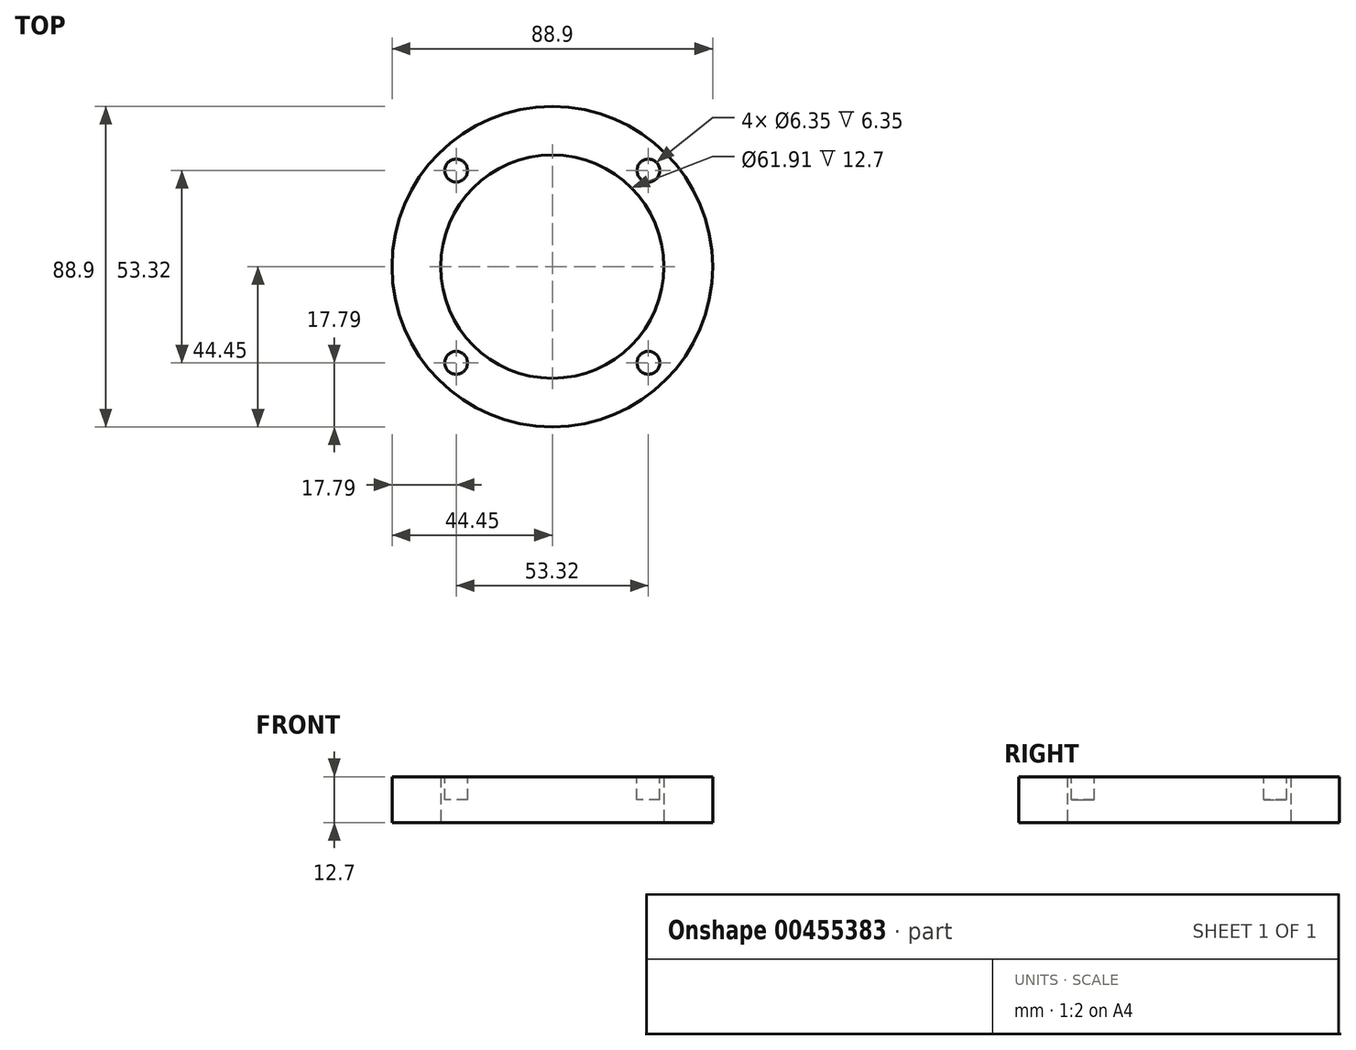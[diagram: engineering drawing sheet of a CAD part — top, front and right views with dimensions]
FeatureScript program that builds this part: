
annotation { "Feature Type Name" : "Feature", "Feature Type Description" : "" }
export const myFeature = defineFeature(function(context is Context, id is Id, definition is map)
    precondition{}
    {
        {
            var Q0;
            Q0=qCreatedBy(makeId("Top.planeOp"),FACE);
            var sketch = newSketch(context, id + "F0", { "sketchPlane" : qUnion([Q0])});
            skCircle(sketch, "E0", {"center": v(0, 0) * mm, "radius": 30.96 * mm});
            skCircle(sketch, "E1", {"center": v(0, 0) * mm, "radius": 44.45 * mm});
            skSolve(sketch);
        }
        {
            var Q0;
            Q0 = qSketchRegion(id + "F0", true);
            extrude(context, id + "F1", {"entities" : qUnion([Q0]), "depth" : 12.7 * mm});
        }
        {
            var Q0;
            Q0=makeQuery(id+"F1.opExtrude","CAP_FACE",FACE,{"disambiguationData":[OSD([sQuery(id+"F0.wireOp",EDGE,"E0"),sQuery(id+"F0.wireOp",EDGE,"E1")])],"isStart":false});
            var sketch = newSketch(context, id + "F2", { "sketchPlane" : qUnion([Q0])});
            skLineSegment(sketch, "E2", {"start": v(0, 0) * mm, "end": v(44.12, 44.12) * mm, "construction": true});
            skCircle(sketch, "E3", {"center": v(26.66, 26.66) * mm, "radius": 3.18 * mm});
            skLineSegment(sketch, "E4", {"start": v(21.89, 21.89) * mm, "end": v(31.43, 31.43) * mm, "construction": true});
            skCircle(sketch, "E5.1.0", {"center": v(-26.66, 26.66) * mm, "radius": 3.18 * mm});
            skCircle(sketch, "E5.2.0", {"center": v(-26.66, -26.66) * mm, "radius": 3.18 * mm});
            skCircle(sketch, "E5.3.0", {"center": v(26.66, -26.66) * mm, "radius": 3.18 * mm});
            skPoint(sketch, "E5.center", {"position": v(0, 0) * mm});
            skSolve(sketch);
        }
        {
            var Q0;
            Q0 = qSketchRegion(id + "F2", true);
            extrude(context, id + "F3", {"entities" : qUnion([Q0]), "operationType" : NewBodyOperationType.REMOVE, "oppositeDirection" : true, "depth" : 6.35 * mm});
        }
    });
